# Revit family: Sink-Single Centre Bowl-Clark Benchmark1
name_source: partatom
category: Plumbing Fixtures
revit_build: Autodesk Revit Architecture 2012 (Build: 20110916_2132(x64)
units: mm (PartAtom-declared; Revit-internal decimal feet)

## types (1)
- Benchmark Single Centre Bowl - 0TH
    1 Taphole = No
    3 Tapholes = No
    Assembly Code = D2010410
    CW Connection = No
    Cost = 0 $
    Default Elevation = 0 mm  [stored 0 ft]
    Depth_ANZRS = 148 mm
    Description = Benchmark Single Centre Bowl LH
    HW Connection = No
    Keynote = SK
    Length_ANZRS = 1234 mm  [stored 4.04856 ft]
    Manufacturer = Clark
    Material_ANZRS = Metal-Stainless-Caroma
    Model = 1012
    Spout Penetation = 100 mm  [stored 0.328084 ft]
    Tap Penetations = 100 mm  [stored 0.328084 ft]
    Type Comments = Includes basket waste, Bowl Volume 13.5L, Carton size 1245 x 475 x 155, Carton weight 5.5kg, Match with Dorf El Toro mixer range
    URL = http://www.clark.com.au
    Vent Connection = No
    WFU = 2
    Waste Connection = Yes
    Waste Radius = 30 mm  [stored 0.0984252 ft]
    Width_ANZRS = 471 mm  [stored 1.54528 ft]

note: [stored X ft] marks values corroborated as IEEE doubles in the binary element streams (Revit-internal decimal feet)

## geometry (parser evidence)
native form markers: Blend x6, Sweep x1
no freeform markers — native parametric forms only
